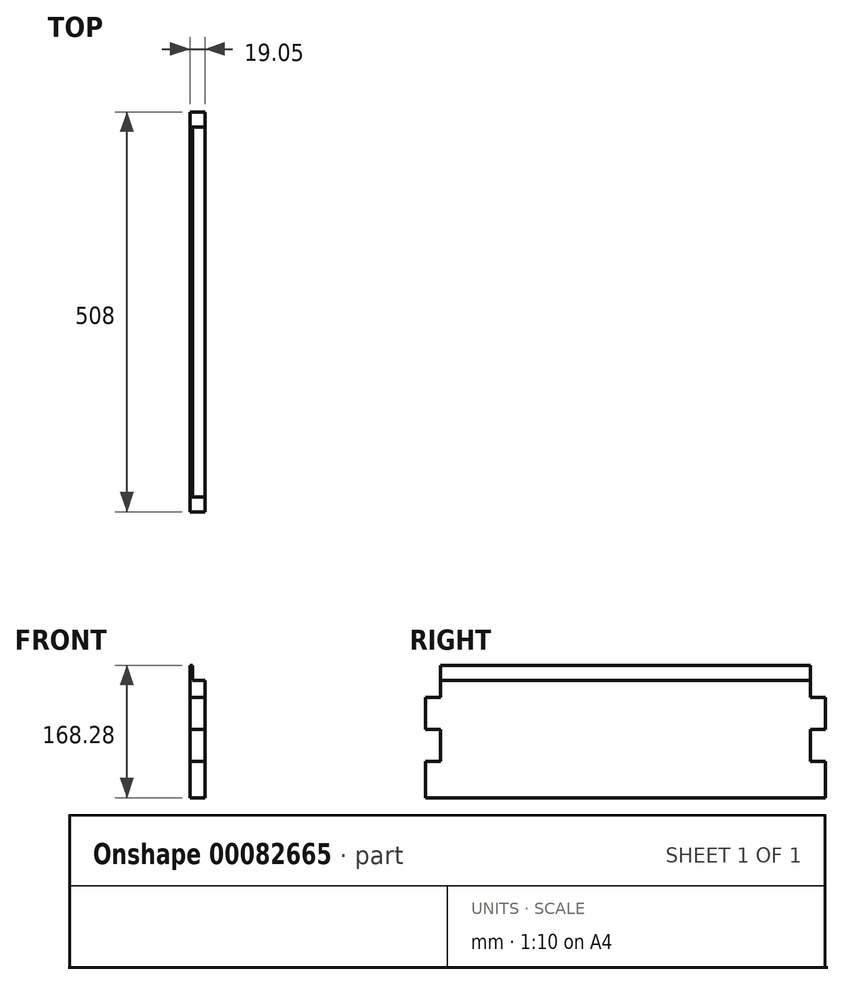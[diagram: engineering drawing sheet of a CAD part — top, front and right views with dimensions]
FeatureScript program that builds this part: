
annotation { "Feature Type Name" : "Feature", "Feature Type Description" : "" }
export const myFeature = defineFeature(function(context is Context, id is Id, definition is map)
    precondition{}
    {
        {
            var Q0;
            Q0=qCreatedBy(makeId("Right.planeOp"),FACE);
            var sketch = newSketch(context, id + "F0", { "sketchPlane" : qUnion([Q0])});
            skLineSegment(sketch, "E0.top", {"start": v(-618.08, -207.98) * mm, "end": v(-599.03, -207.98) * mm});
            skLineSegment(sketch, "E1.top", {"start": v(-618.08, -248.62) * mm, "end": v(-599.03, -248.62) * mm});
            skLineSegment(sketch, "E1.left", {"start": v(-618.08, -207.98) * mm, "end": v(-618.08, -248.62) * mm});
            skLineSegment(sketch, "E2.top", {"start": v(-618.08, -289.26) * mm, "end": v(-599.03, -289.26) * mm});
            skLineSegment(sketch, "E2.right", {"start": v(-599.03, -248.62) * mm, "end": v(-599.03, -289.26) * mm});
            skLineSegment(sketch, "E3.left", {"start": v(-618.08, -289.26) * mm, "end": v(-618.08, -335.62) * mm});
            skLineSegment(sketch, "E4.MirrorCS", {"start": v(-110.08, -289.26) * mm, "end": v(-129.13, -289.26) * mm});
            skLineSegment(sketch, "E5.MirrorCS", {"start": v(-110.08, -207.98) * mm, "end": v(-129.13, -207.98) * mm});
            skLineSegment(sketch, "E6.MirrorCS", {"start": v(-110.08, -248.62) * mm, "end": v(-129.13, -248.62) * mm});
            skLineSegment(sketch, "E7.MirrorCS", {"start": v(-110.08, -289.26) * mm, "end": v(-110.08, -335.62) * mm});
            skLineSegment(sketch, "E8.MirrorCS", {"start": v(-110.08, -207.98) * mm, "end": v(-110.08, -248.62) * mm});
            skLineSegment(sketch, "E9.MirrorCS", {"start": v(-129.13, -248.62) * mm, "end": v(-129.13, -289.26) * mm});
            skLineSegment(sketch, "E10", {"start": v(-129.13, -167.34) * mm, "end": v(-599.03, -167.34) * mm});
            skLineSegment(sketch, "E11", {"start": v(-364.08, -167.34) * mm, "end": v(-364.08, -335.62) * mm, "construction": true});
            skLineSegment(sketch, "E12", {"start": v(-599.03, -167.34) * mm, "end": v(-599.03, -207.98) * mm});
            skLineSegment(sketch, "E13", {"start": v(-129.13, -167.34) * mm, "end": v(-129.13, -207.98) * mm});
            skLineSegment(sketch, "E14", {"start": v(-618.08, -335.62) * mm, "end": v(-110.08, -335.62) * mm});
            skSolve(sketch);
        }
        {
            var Q0;
            Q0=makeQuery(id+"F0.imprint","IMPRINT",FACE,{"disambiguationData":[TD([[makeQuery(id+"F0.imprint","IMPRINT",EDGE,{"derivedFrom":sQuery(id+"F0.wireOp",EDGE,"26864448-1c94-45d2-b1b5-f008a4c91ff0.right")}),1.0]])]});
            var Q1;
            Q1=makeQuery(id+"F0.imprint","IMPRINT",FACE,{"disambiguationData":[TD([[makeQuery(id+"F0.imprint","IMPRINT",EDGE,{"derivedFrom":sQuery(id+"F0.wireOp",EDGE,"E0.top")}),-1.0]])]});
            extrude(context, id + "F1", {"entities" : qUnion([Q0, Q1]), "depth" : 19.05 * mm});
        }
        {
            var Q0;
            Q0=makeQuery(id+"F1.opExtrude","CAP_FACE",FACE,{"disambiguationData":[OSD([sQuery(id+"F0.wireOp",EDGE,"26864448-1c94-45d2-b1b5-f008a4c91ff0.right"),sQuery(id+"F0.wireOp",EDGE,"c4c25887-50d7-47ce-89de-4f48a683c6e8.bottom"),sQuery(id+"F0.wireOp",EDGE,"c4c25887-50d7-47ce-89de-4f48a683c6e8.left"),sQuery(id+"F0.wireOp",EDGE,"E0.bottom"),sQuery(id+"F0.wireOp",EDGE,"E0.right"),sQuery(id+"F0.wireOp",EDGE,"E0.top"),sQuery(id+"F0.wireOp",EDGE,"E1.left"),sQuery(id+"F0.wireOp",EDGE,"E1.top"),sQuery(id+"F0.wireOp",EDGE,"E2.right"),sQuery(id+"F0.wireOp",EDGE,"E2.top"),sQuery(id+"F0.wireOp",EDGE,"E3.top"),sQuery(id+"F0.wireOp",EDGE,"E3.left"),sQuery(id+"F0.wireOp",EDGE,"E7.MirrorCS"),sQuery(id+"F0.wireOp",EDGE,"bca2cd61-a9a2-4b3e-8558-699204f67ddb.MirrorCS"),sQuery(id+"F0.wireOp",EDGE,"E8.MirrorCS"),sQuery(id+"F0.wireOp",EDGE,"E4.MirrorCS"),sQuery(id+"F0.wireOp",EDGE,"cc5dd828-1f3e-4a7d-88fd-949d9d13e1f3.MirrorCS"),sQuery(id+"F0.wireOp",EDGE,"dcadf4c2-bc20-4a87-959d-c3d3b32e47b1.MirrorCS"),sQuery(id+"F0.wireOp",EDGE,"6d50509d-a2dd-471e-a44f-27f8866fe290.MirrorCS"),sQuery(id+"F0.wireOp",EDGE,"E6.MirrorCS"),sQuery(id+"F0.wireOp",EDGE,"E5.MirrorCS"),sQuery(id+"F0.wireOp",EDGE,"E9.MirrorCS"),sQuery(id+"F0.wireOp",EDGE,"2afa2a2b-48d4-4b8e-8132-1fdea11e696a.MirrorCS"),sQuery(id+"F0.wireOp",EDGE,"3257c890-601a-471a-8d31-b63cc1e1203e.MirrorCS"),sQuery(id+"F0.wireOp",EDGE,"E10"),sQuery(id+"F0.wireOp",EDGE,"Yiaemo1m-Cym1-rf2j-Mf2j-aFuqPHo4yuLP")])],"isStart":false});
            var sketch = newSketch(context, id + "F2", { "sketchPlane" : qUnion([Q0])});
            skLineSegment(sketch, "E15", {"start": v(-129.13, -167.34) * mm, "end": v(-129.13, -186.4) * mm});
            skLineSegment(sketch, "E16", {"start": v(-129.13, -186.4) * mm, "end": v(-129.13, -186.4) * mm});
            skLineSegment(sketch, "E17", {"start": v(-129.13, -186.4) * mm, "end": v(-129.13, -167.34) * mm});
            skLineSegment(sketch, "E18", {"start": v(-129.13, -167.34) * mm, "end": v(-129.13, -167.34) * mm});
            skLineSegment(sketch, "E19", {"start": v(-129.13, -186.4) * mm, "end": v(-599.03, -186.4) * mm});
            skLineSegment(sketch, "E20", {"start": v(-599.03, -186.4) * mm, "end": v(-599.03, -167.34) * mm});
            skLineSegment(sketch, "E21", {"start": v(-599.03, -167.34) * mm, "end": v(-129.13, -167.34) * mm});
            skSolve(sketch);
        }
        {
            var Q0;
            Q0=qSketchRegion(id+"F2",true);
            extrude(context, id + "F3", {"entities" : qUnion([Q0]), "operationType" : NewBodyOperationType.REMOVE, "oppositeDirection" : true, "depth" : 15.88 * mm});
        }
    });
